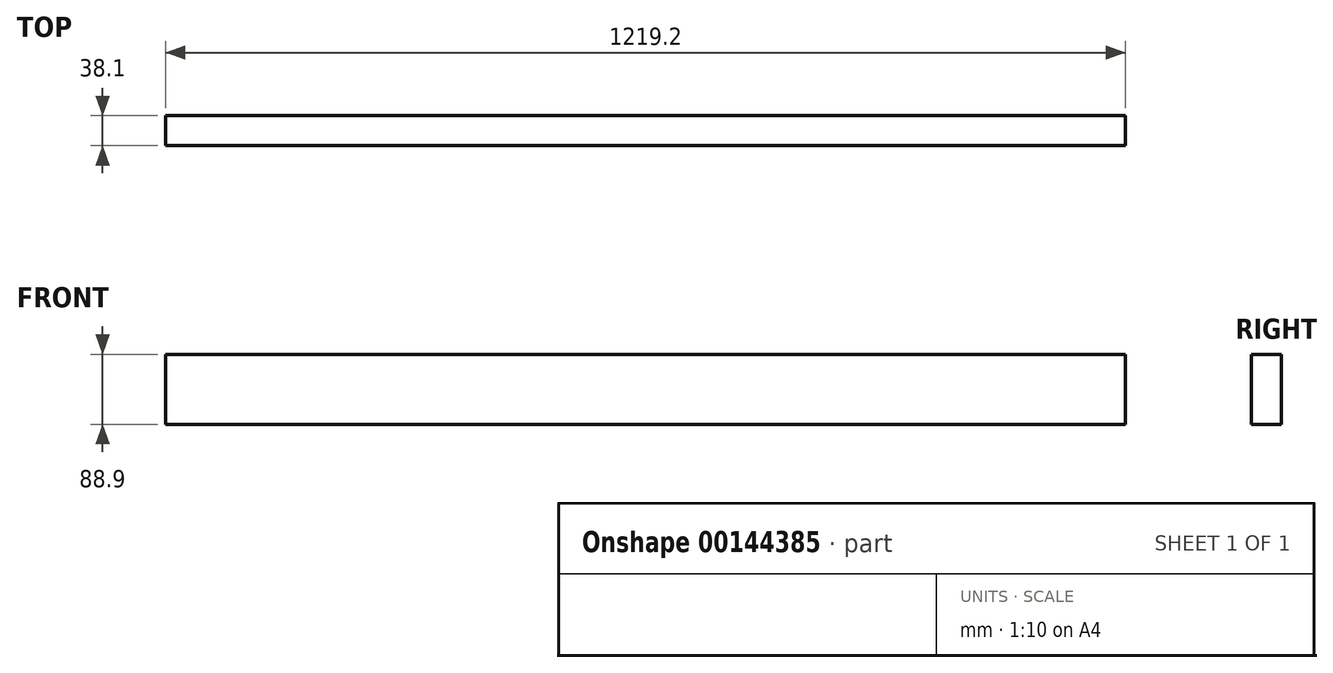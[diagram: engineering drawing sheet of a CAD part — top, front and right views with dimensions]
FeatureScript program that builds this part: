
annotation { "Feature Type Name" : "Feature", "Feature Type Description" : "" }
export const myFeature = defineFeature(function(context is Context, id is Id, definition is map)
    precondition{}
    {
        {
            var Q0;
            Q0=qCreatedBy(makeId("Top.planeOp"),FACE);
            var sketch = newSketch(context, id + "F0", { "sketchPlane" : qUnion([Q0])});
            skLineSegment(sketch, "E0.bottom", {"start": v(-609.6, -19.05) * mm, "end": v(609.6, -19.05) * mm});
            skLineSegment(sketch, "E0.top", {"start": v(-609.6, 19.05) * mm, "end": v(609.6, 19.05) * mm});
            skLineSegment(sketch, "E0.left", {"start": v(-609.6, -19.05) * mm, "end": v(-609.6, 19.05) * mm});
            skLineSegment(sketch, "E0.right", {"start": v(609.6, -19.05) * mm, "end": v(609.6, 19.05) * mm});
            skPoint(sketch, "E0.middle", {"position": v(0, 0) * mm});
            skSolve(sketch);
        }
        {
            var Q0;
            Q0=qSketchRegion(id+"F0",true);
            extrude(context, id + "F1", {"entities" : qUnion([Q0]), "depth" : 88.9 * mm});
        }
    });
